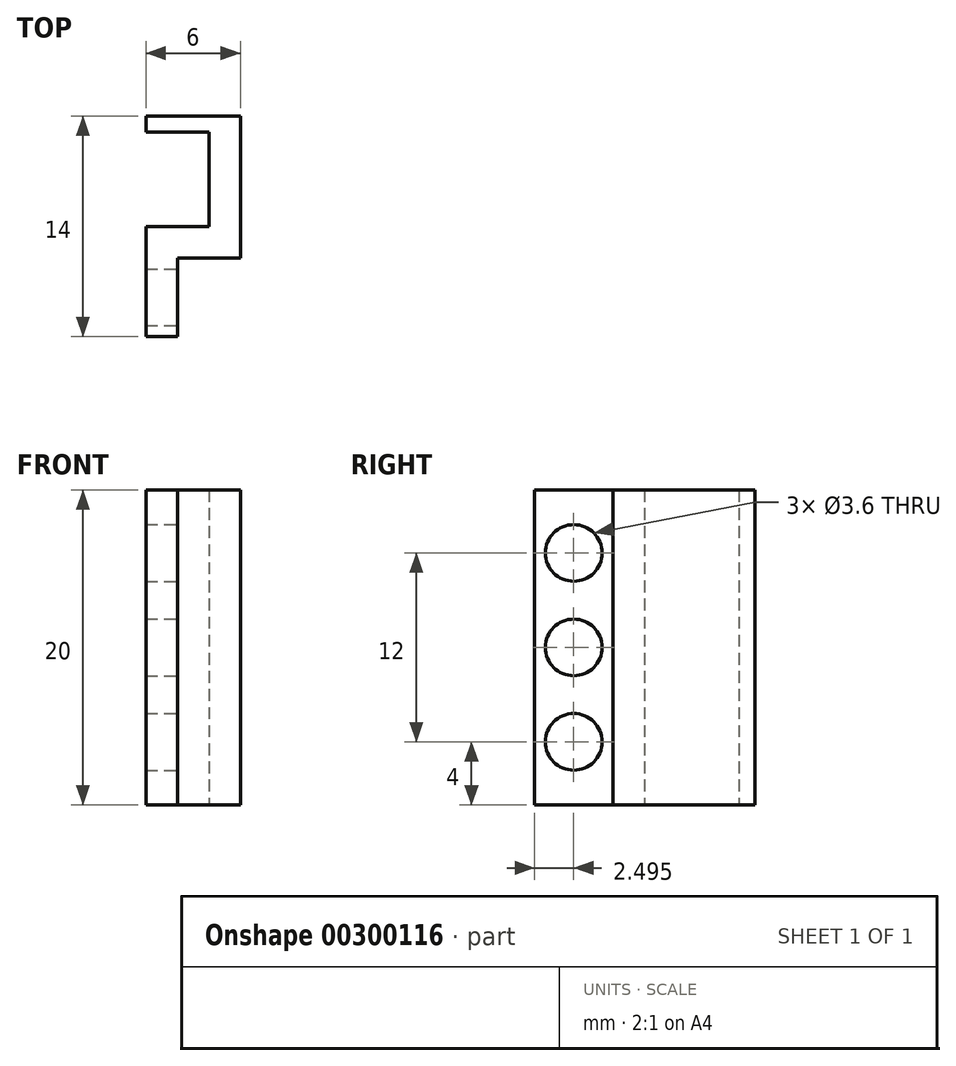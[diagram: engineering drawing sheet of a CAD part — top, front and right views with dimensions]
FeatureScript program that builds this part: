
annotation { "Feature Type Name" : "Feature", "Feature Type Description" : "" }
export const myFeature = defineFeature(function(context is Context, id is Id, definition is map)
    precondition{}
    {
        {
            var Q0;
            Q0=qCreatedBy(makeId("Top.planeOp"),FACE);
            var sketch = newSketch(context, id + "F0", { "sketchPlane" : qUnion([Q0])});
            skLineSegment(sketch, "E0", {"start": v(7.33, -1.2) * mm, "end": v(7.33, -10.2) * mm});
            skLineSegment(sketch, "E1", {"start": v(7.33, -10.2) * mm, "end": v(3.33, -10.2) * mm});
            skLineSegment(sketch, "E2", {"start": v(3.33, -10.2) * mm, "end": v(3.33, -15.2) * mm});
            skLineSegment(sketch, "E3", {"start": v(5.33, -8.2) * mm, "end": v(1.33, -8.2) * mm});
            skLineSegment(sketch, "E4", {"start": v(1.33, -8.2) * mm, "end": v(1.33, -15.2) * mm});
            skLineSegment(sketch, "E5", {"start": v(1.33, -15.2) * mm, "end": v(3.33, -15.2) * mm});
            skLineSegment(sketch, "E6", {"start": v(1.33, -1.2) * mm, "end": v(1.33, -2.2) * mm});
            skLineSegment(sketch, "E7", {"start": v(1.33, -2.2) * mm, "end": v(5.33, -2.2) * mm});
            skLineSegment(sketch, "E8", {"start": v(5.33, -2.2) * mm, "end": v(5.33, -8.2) * mm});
            skLineSegment(sketch, "E9", {"start": v(7.33, -1.2) * mm, "end": v(1.33, -1.2) * mm});
            skSolve(sketch);
        }
        {
            var Q0;
            Q0=makeQuery(id+"F0.imprint","IMPRINT",FACE,{"disambiguationData":[TD([[makeQuery(id+"F0.imprint","IMPRINT",EDGE,{"derivedFrom":sQuery(id+"F0.wireOp",EDGE,"E0")}),-1.0]])]});
            extrude(context, id + "F1", {"entities" : qUnion([Q0]), "depth" : 20 * mm});
        }
        {
            var Q0;
            Q0=makeQuery(id+"F1.opExtrude","SWEPT_FACE",FACE,{"disambiguationData":[OSD([sQuery(id+"F0.wireOp",EDGE,"E2")])]});
            var sketch = newSketch(context, id + "F2", { "sketchPlane" : qUnion([Q0])});
            skLineSegment(sketch, "E10", {"start": v(-12.7, 0) * mm, "end": v(-12.7, 20) * mm, "construction": true});
            skLineSegment(sketch, "E11", {"start": v(-10.2, 16) * mm, "end": v(-15.2, 16) * mm, "construction": true});
            skLineSegment(sketch, "E12", {"start": v(-10.2, 4) * mm, "end": v(-15.2, 4) * mm, "construction": true});
            skLineSegment(sketch, "E13", {"start": v(-10.2, 10) * mm, "end": v(-15.2, 10) * mm, "construction": true});
            skCircle(sketch, "E14", {"center": v(-12.7, 10) * mm, "radius": 1.8 * mm});
            skCircle(sketch, "E15", {"center": v(-12.7, 4) * mm, "radius": 1.8 * mm});
            skCircle(sketch, "E16", {"center": v(-12.7, 16) * mm, "radius": 1.8 * mm});
            skSolve(sketch);
        }
        {
            var Q0;
            Q0=makeQuery(id+"F2.imprint","IMPRINT",FACE,{"disambiguationData":[TD([[makeQuery(id+"F2.imprint","IMPRINT",EDGE,{"derivedFrom":sQuery(id+"F2.wireOp",EDGE,"E16")}),1.0]])]});
            var Q1;
            Q1=makeQuery(id+"F2.imprint","IMPRINT",FACE,{"disambiguationData":[TD([[makeQuery(id+"F2.imprint","IMPRINT",EDGE,{"derivedFrom":sQuery(id+"F2.wireOp",EDGE,"E14")}),1.0]])]});
            var Q2;
            Q2=makeQuery(id+"F2.imprint","IMPRINT",FACE,{"disambiguationData":[TD([[makeQuery(id+"F2.imprint","IMPRINT",EDGE,{"derivedFrom":sQuery(id+"F2.wireOp",EDGE,"E15")}),1.0]])]});
            extrude(context, id + "F3", {"entities" : qUnion([Q0, Q1, Q2]), "operationType" : NewBodyOperationType.REMOVE, "oppositeDirection" : true, "depth" : 25 * mm});
        }
    });
